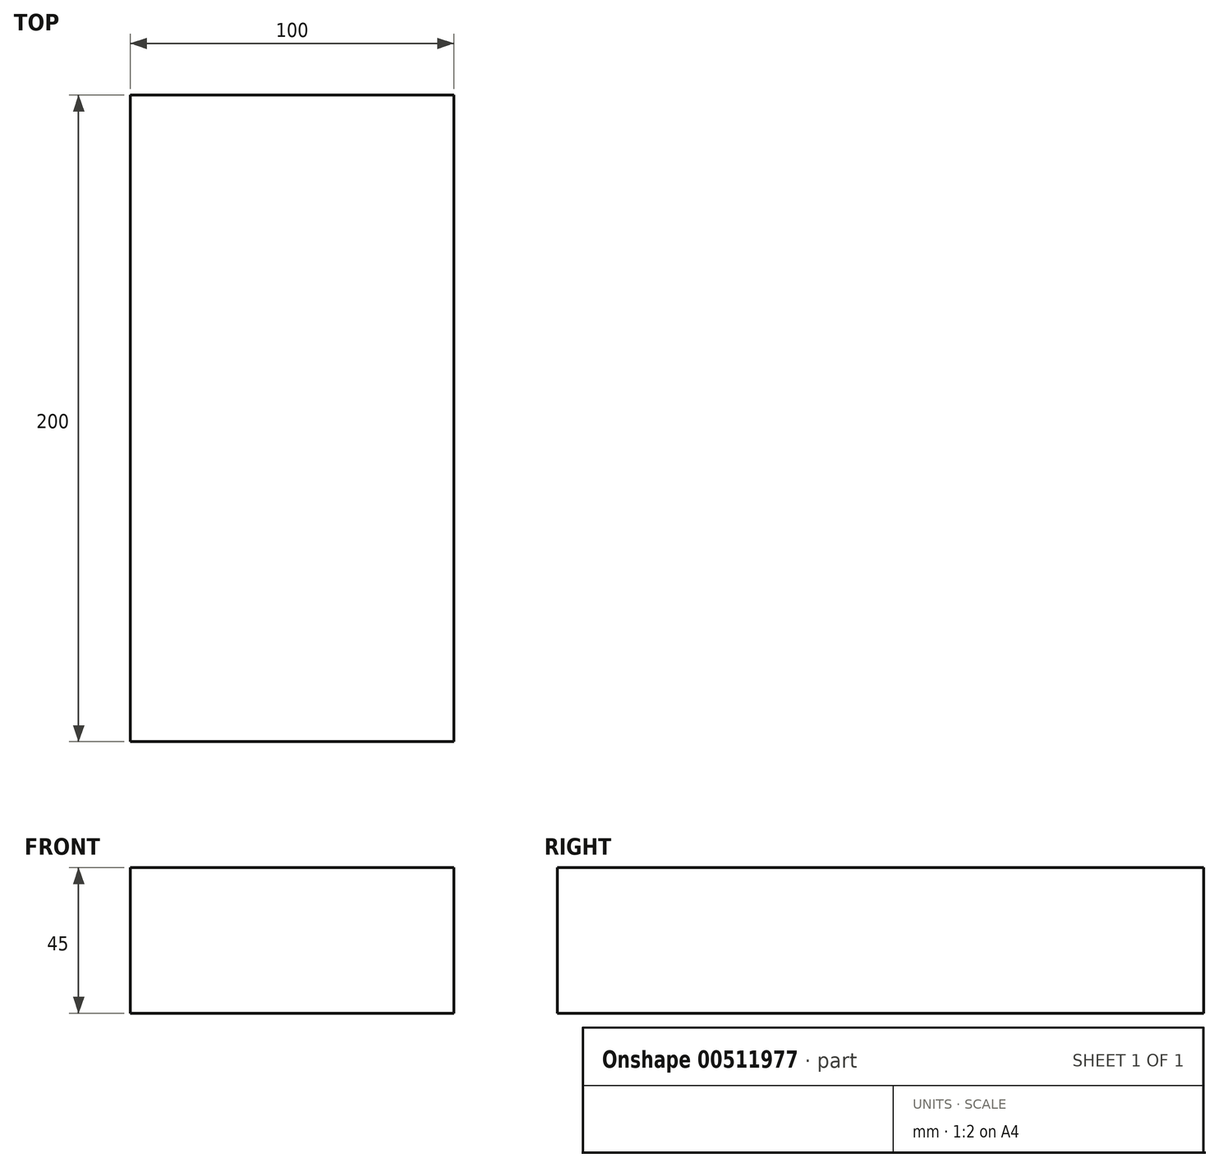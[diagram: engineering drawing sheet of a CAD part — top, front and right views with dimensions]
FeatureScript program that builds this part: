
annotation { "Feature Type Name" : "Feature", "Feature Type Description" : "" }
export const myFeature = defineFeature(function(context is Context, id is Id, definition is map)
    precondition{}
    {
        {
            var Q0;
            Q0=qCreatedBy(makeId("Top.planeOp"),FACE);
            var sketch = newSketch(context, id + "F0", { "sketchPlane" : qUnion([Q0])});
            skLineSegment(sketch, "E0.bottom", {"start": v(50, -100) * mm, "end": v(-50, -100) * mm});
            skLineSegment(sketch, "E0.top", {"start": v(50, 100) * mm, "end": v(-50, 100) * mm});
            skLineSegment(sketch, "E0.left", {"start": v(50, -100) * mm, "end": v(50, 100) * mm});
            skLineSegment(sketch, "E0.right", {"start": v(-50, -100) * mm, "end": v(-50, 100) * mm});
            skPoint(sketch, "E0.middle", {"position": v(0, 0) * mm});
            skSolve(sketch);
        }
        {
            var Q0;
            Q0=makeQuery(id+"F0.imprint","IMPRINT",FACE,{"disambiguationData":[TD([[makeQuery(id+"F0.imprint","IMPRINT",EDGE,{"derivedFrom":sQuery(id+"F0.wireOp",EDGE,"E0.bottom")}),-1.0]])]});
            extrude(context, id + "F1", {"entities" : qUnion([Q0]), "depth" : 45 * mm});
        }
    });
